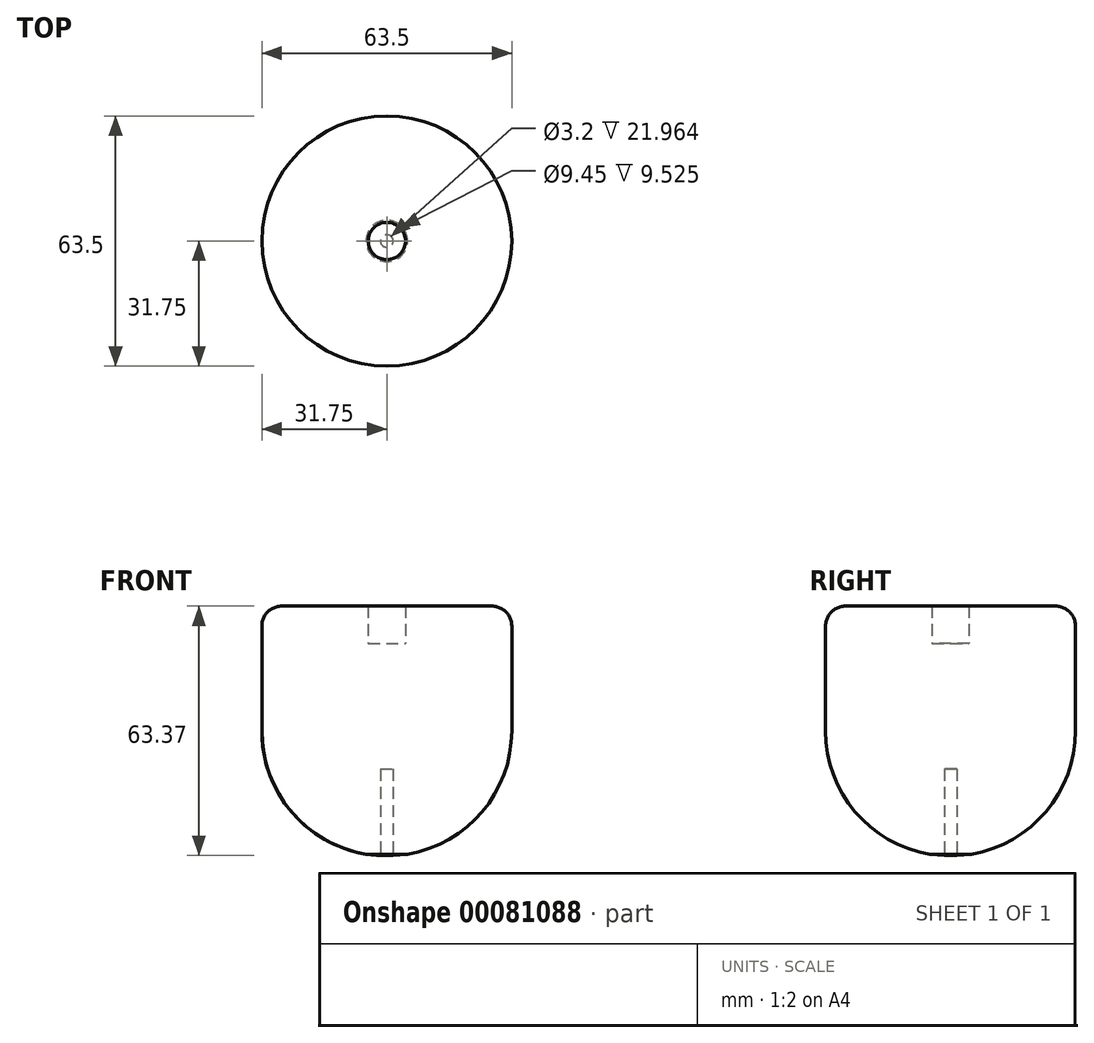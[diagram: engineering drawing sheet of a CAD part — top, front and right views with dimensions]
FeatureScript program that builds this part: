
annotation { "Feature Type Name" : "Feature", "Feature Type Description" : "" }
export const myFeature = defineFeature(function(context is Context, id is Id, definition is map)
    precondition{}
    {
        {
            var Q0;
            Q0=qCreatedBy(makeId("Front.planeOp"),FACE);
            var sketch = newSketch(context, id + "F0", { "sketchPlane" : qUnion([Q0])});
            skLineSegment(sketch, "E0", {"start": v(0, 0) * mm, "end": v(0, 16.51) * mm});
            skLineSegment(sketch, "E1", {"start": v(0, 0) * mm, "end": v(0, -27.94) * mm});
            skLineSegment(sketch, "E2", {"start": v(0, -27.94) * mm, "end": v(0, 35.56) * mm});
            skLineSegment(sketch, "E3", {"start": v(-4.72, 35.56) * mm, "end": v(-4.72, 26.03) * mm});
            skLineSegment(sketch, "E4", {"start": v(-4.72, 35.56) * mm, "end": v(-7.26, 35.56) * mm});
            skLineSegment(sketch, "E5", {"start": v(0, 35.56) * mm, "end": v(0, 26.03) * mm});
            skLineSegment(sketch, "E6", {"start": v(0, 26.03) * mm, "end": v(-4.72, 26.03) * mm});
            skPoint(sketch, "E7", {"position": v(-7.26, -3.67) * mm});
            skPoint(sketch, "E8", {"position": v(-16.16, -5.93) * mm});
            skPoint(sketch, "E9", {"position": v(-24.25, -7.55) * mm});
            skLineSegment(sketch, "E10", {"start": v(-24.25, -7.55) * mm, "end": v(-24.25, -7.55) * mm});
            skPoint(sketch, "E11", {"position": v(-24.43, 6.97) * mm});
            skPoint(sketch, "E12.3.internal.snap0", {"position": v(7.64, 16.51) * mm});
            skLineSegment(sketch, "E13", {"start": v(-1.6, -27.8) * mm, "end": v(-5.26, -27.5) * mm});
            skLineSegment(sketch, "E14", {"start": v(0, -27.94) * mm, "end": v(0, -5.84) * mm});
            skLineSegment(sketch, "E15", {"start": v(0, -5.84) * mm, "end": v(-1.6, -5.84) * mm});
            skLineSegment(sketch, "E16", {"start": v(-1.6, -5.84) * mm, "end": v(-1.6, -27.8) * mm});
            skFitSpline(sketch, "E17.trimOffspring", {"points": [v(-24.43, 6.97) * mm, v(-7.26, 12.37) * mm, v(-9.1, 16.51) * mm], "startDerivative": vector(32.41, -14.69) * mm, "endDerivative": vector(-11.55, 14.27) * mm});
            skLineSegment(sketch, "E18", {"start": v(0, -27.94) * mm, "end": v(0, 3.8) * mm});
            skLineSegment(sketch, "E19", {"start": v(-7.26, 35.56) * mm, "end": v(-31.75, 35.56) * mm});
            skLineSegment(sketch, "E20", {"start": v(-31.75, 35.56) * mm, "end": v(-31.75, 3.8) * mm});
            skLineSegment(sketch, "E21", {"start": v(-1.6, -27.8) * mm, "end": v(-1.6, -27.9) * mm});
            skArc(sketch, "E22.trimOffspring", {"start": v(-31.75, 3.8) * mm, "mid": v(-23, -18.07) * mm, "end": v(-1.6, -27.9) * mm});
            skPoint(sketch, "E23.end.orphan", {"position": v(-7.26, 16.51) * mm});
            skPoint(sketch, "E24.orphan", {"position": v(22.54, 16.51) * mm});
            skSolve(sketch);
        }
        {
            var Q0;
            {var subQ0=sQuery(id+"F0.wireOp",EDGE,"E10");var subQ1=sQuery(id+"F0.wireOp",EDGE,"tVGfZYd6-jjf8-WeDL-8lbz-A1Di6X17U0wS");var subQ2=makeQuery(id+"F0.imprint","INTERSECT",VERTEX,{"disambiguationData":[OD(0.0)],"derivedFrom":[subQ1,subQ0]});Q0=makeQuery(id+"F0.imprint","IMPRINT",FACE,{"disambiguationData":[TD([[makeQuery(id+"F0.imprint","IMPRINT",EDGE,{"disambiguationData":[TD([[subQ2,-1.0]])],"derivedFrom":subQ1}),1.0]])]});}
            var Q1;
            {var subQ0=sQuery(id+"F0.wireOp",EDGE,"tVGfZYd6-jjf8-WeDL-8lbz-A1Di6X17U0wS");var subQ1=sQuery(id+"F0.wireOp",EDGE,"bDiMBlMv-fEZ2-t5qV-gFNT-cdJ1VpS5pjVa");var subQ2=makeQuery(id+"F0.imprint","INTERSECT",VERTEX,{"derivedFrom":[subQ1,subQ0]});Q1=makeQuery(id+"F0.imprint","IMPRINT",FACE,{"disambiguationData":[TD([[makeQuery(id+"F0.imprint","IMPRINT",EDGE,{"disambiguationData":[TD([[subQ2,1.0]])],"derivedFrom":subQ1}),1.0]])]});}
            var Q2;
            {var subQ0=sQuery(id+"F0.wireOp",EDGE,"E6");Q2=makeQuery(id+"F0.imprint","IMPRINT",FACE,{"disambiguationData":[TD([[makeQuery(id+"F0.imprint","IMPRINT",EDGE,{"derivedFrom":subQ0}),1.0]])]});}
            var Q3;
            {var subQ1=sQuery(id+"F0.wireOp",EDGE,"E4");Q3=makeQuery(id+"F0.imprint","IMPRINT",FACE,{"disambiguationData":[TD([[makeQuery(id+"F0.imprint","IMPRINT",EDGE,{"derivedFrom":subQ1}),1.0]])]});}
            var Q4;
            {var subQ4=sQuery(id+"F0.wireOp",EDGE,"738dc5bb-a17f-4ab5-bc4a-0e76f5a0ee42.trimOffspring");Q4=makeQuery(id+"F0.imprint","IMPRINT",FACE,{"disambiguationData":[TD([[makeQuery(id+"F0.imprint","IMPRINT",EDGE,{"derivedFrom":subQ4}),1.0]])]});}
            var Q5;
            {var subQ0=sQuery(id+"F0.wireOp",EDGE,"E2");var subQ1=makeQuery(id+"F0.imprint","IMPRINT",VERTEX,{"derivedFrom":subQ0});Q5=makeQuery(id+"F0.imprint","IMPRINT",FACE,{"disambiguationData":[TD([[makeQuery(id+"F0.imprint","IMPRINT",EDGE,{"disambiguationData":[TD([[subQ1,1.0]])],"derivedFrom":subQ0}),1.0]])]});}
            var Q6;
            {var subQ1=sQuery(id+"F0.wireOp",EDGE,"bDiMBlMv-fEZ2-t5qV-gFNT-cdJ1VpS5pjVa");var subQ8=sQuery(id+"F0.wireOp",EDGE,"E3");var subQ9=makeQuery(id+"F0.imprint","INTERSECT",VERTEX,{"derivedFrom":[subQ1,subQ8]});Q6=makeQuery(id+"F0.imprint","IMPRINT",FACE,{"disambiguationData":[TD([[makeQuery(id+"F0.imprint","IMPRINT",EDGE,{"disambiguationData":[TD([[subQ9,1.0]])],"derivedFrom":subQ1}),1.0]])]});}
            var Q7;
            Q7=sQuery(id+"F0.wireOp",EDGE,"E2");
            revolve(context, id + "F1", {"entities" : qUnion([Q0, Q1, Q2, Q3, Q4, Q5, Q6]), "axis" : qUnion([Q7]), "revolveType" : RevolveType.FULL});
        }
        {
            var Q0;
            {var subQ0=sQuery(id+"F0.wireOp",EDGE,"E19");Q0=makeQuery(id+"F0.imprint","IMPRINT",FACE,{"disambiguationData":[TD([[makeQuery(id+"F0.imprint","IMPRINT",EDGE,{"derivedFrom":subQ0}),1.0]])]});}
            var Q1;
            {var subQ0=sQuery(id+"F0.wireOp",EDGE,"bmbKWJhc-LnRI-lJPz-WfQc-znhdkw0a0RDT");var subQ1=sQuery(id+"F0.wireOp",EDGE,"lUbTEnaK-Ua1a-NUB4-kNsj-y0ZaYhOh5Trz");var subQ2=makeQuery(id+"F0.imprint","INTERSECT",VERTEX,{"derivedFrom":[subQ1,subQ0]});Q1=makeQuery(id+"F0.imprint","IMPRINT",FACE,{"disambiguationData":[TD([[makeQuery(id+"F0.imprint","IMPRINT",EDGE,{"disambiguationData":[TD([[subQ2,-1.0]])],"derivedFrom":subQ1}),-1.0]])]});}
            var Q2;
            {var subQ7=sQuery(id+"F0.wireOp",EDGE,"lUbTEnaK-Ua1a-NUB4-kNsj-y0ZaYhOh5Trz");var subQ12=sQuery(id+"F0.wireOp",EDGE,"bmbKWJhc-LnRI-lJPz-WfQc-znhdkw0a0RDT");var subQ14=makeQuery(id+"F0.imprint","INTERSECT",VERTEX,{"derivedFrom":[subQ7,subQ12]});Q2=makeQuery(id+"F0.imprint","IMPRINT",FACE,{"disambiguationData":[TD([[makeQuery(id+"F0.imprint","IMPRINT",EDGE,{"disambiguationData":[TD([[subQ14,-1.0]])],"derivedFrom":subQ7}),1.0]])]});}
            var Q3;
            {var subQ0=sQuery(id+"F0.wireOp",EDGE,"E13");var subQ1=sQuery(id+"F0.wireOp",EDGE,"lUbTEnaK-Ua1a-NUB4-kNsj-y0ZaYhOh5Trz");var subQ2=makeQuery(id+"F0.imprint","INTERSECT",VERTEX,{"derivedFrom":[subQ1,subQ0]});Q3=makeQuery(id+"F0.imprint","IMPRINT",FACE,{"disambiguationData":[TD([[makeQuery(id+"F0.imprint","IMPRINT",EDGE,{"disambiguationData":[TD([[subQ2,1.0]])],"derivedFrom":subQ1}),-1.0]])]});}
            var Q4;
            {var subQ1=sQuery(id+"F0.wireOp",EDGE,"E15");Q4=makeQuery(id+"F0.imprint","IMPRINT",FACE,{"disambiguationData":[TD([[makeQuery(id+"F0.imprint","IMPRINT",EDGE,{"derivedFrom":subQ1}),-1.0]])]});}
            var Q5;
            Q5=sQuery(id+"F0.wireOp",EDGE,"E2");
            revolve(context, id + "F2", {"entities" : qUnion([Q0, Q1, Q2, Q3, Q4]), "axis" : qUnion([Q5]), "revolveType" : RevolveType.FULL});
        }
        {
            var Q0;
            Q0=makeQuery(id+"F2.opRevolve","SWEPT_EDGE",EDGE,{"disambiguationData":[OSD([sQuery(id+"F0.wireOp",EDGE,"E19"),sQuery(id+"F0.wireOp",EDGE,"E20")])]});
            fillet(context, id + "F3", {"entities" : qUnion([Q0]), "radius" : 5.08 * mm, "tangentPropagation" : true, "allowEdgeOverflow" : false});
        }
        {
            var Q0;
            Q0=makeQuery(id+"F2.opRevolve","SWEPT_BODY",BODY,{"disambiguationData":[OSD([sQuery(id+"F0.wireOp",EDGE,"E2"),sQuery(id+"F0.wireOp",EDGE,"E3"),sQuery(id+"F0.wireOp",EDGE,"E4"),sQuery(id+"F0.wireOp",EDGE,"E6"),sQuery(id+"F0.wireOp",EDGE,"E13"),sQuery(id+"F0.wireOp",EDGE,"E15"),sQuery(id+"F0.wireOp",EDGE,"E16"),sQuery(id+"F0.wireOp",EDGE,"E18"),sQuery(id+"F0.wireOp",EDGE,"E19"),sQuery(id+"F0.wireOp",EDGE,"E20"),sQuery(id+"F0.wireOp",EDGE,"E22.trimOffspring")])]});
            deleteBodies(context, id + "F4", {"entities" : qUnion([Q0])});
        }
        {
            var Q0;
            Q0=makeQuery(id+"F1.opRevolve","SWEPT_EDGE",EDGE,{"disambiguationData":[OSD([sQuery(id+"F0.wireOp",EDGE,"E19"),sQuery(id+"F0.wireOp",EDGE,"E20")])]});
            fillet(context, id + "F5", {"entities" : qUnion([Q0]), "radius" : 5.08 * mm, "tangentPropagation" : true, "allowEdgeOverflow" : false});
        }
    });
